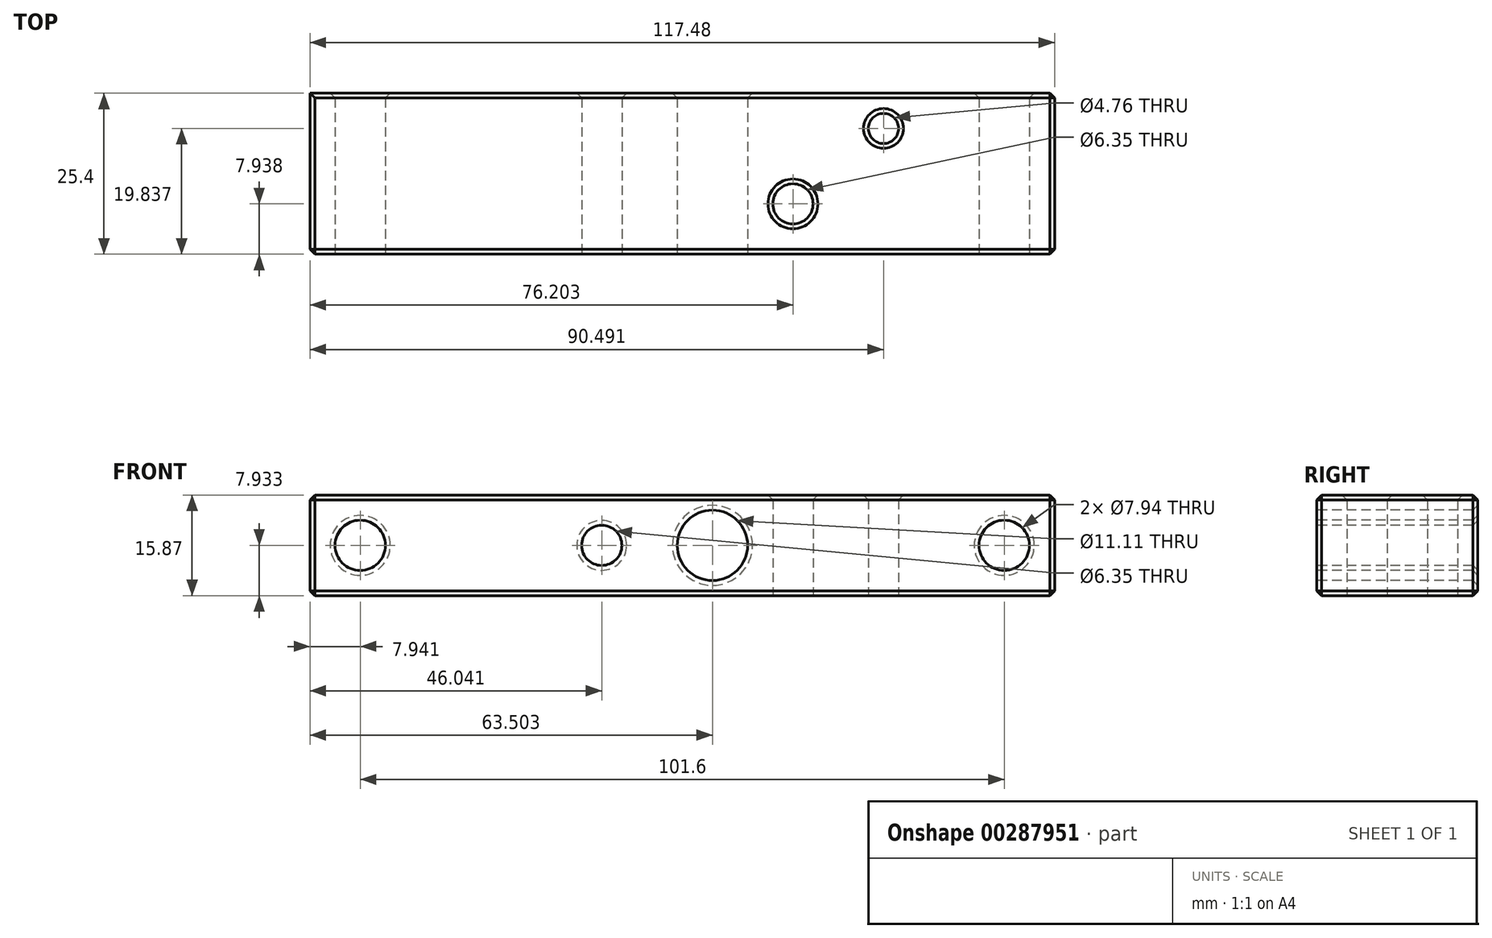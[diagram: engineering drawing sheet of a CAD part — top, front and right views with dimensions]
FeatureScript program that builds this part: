
annotation { "Feature Type Name" : "Feature", "Feature Type Description" : "" }
export const myFeature = defineFeature(function(context is Context, id is Id, definition is map)
    precondition{}
    {
        {
            var Q0;
            Q0=qCreatedBy(makeId("Front.planeOp"),FACE);
            var sketch = newSketch(context, id + "F0", { "sketchPlane" : qUnion([Q0])});
            skLineSegment(sketch, "E0.bottom", {"start": v(-99.14, 37.25) * mm, "end": v(18.34, 37.25) * mm});
            skLineSegment(sketch, "E0.top", {"start": v(-99.14, 21.38) * mm, "end": v(18.34, 21.38) * mm});
            skLineSegment(sketch, "E0.left", {"start": v(-99.14, 37.25) * mm, "end": v(-99.14, 21.38) * mm});
            skLineSegment(sketch, "E0.right", {"start": v(18.34, 37.25) * mm, "end": v(18.34, 21.38) * mm});
            skSolve(sketch);
        }
        {
            var Q0;
            Q0=makeQuery(id+"F0.imprint","IMPRINT",FACE,{"disambiguationData":[TD([[makeQuery(id+"F0.imprint","IMPRINT",EDGE,{"derivedFrom":sQuery(id+"F0.wireOp",EDGE,"E0.bottom")}),-1.0]])]});
            extrude(context, id + "F1", {"entities" : qUnion([Q0]), "depth" : 25.4 * mm, "offsetDistance" : 25.4 * mm});
        }
        {
            var Q0;
            Q0=makeQuery(id+"F1.opExtrude","CAP_FACE",FACE,{"disambiguationData":[OSD([sQuery(id+"F0.wireOp",EDGE,"E0.bottom"),sQuery(id+"F0.wireOp",EDGE,"E0.top"),sQuery(id+"F0.wireOp",EDGE,"E0.left"),sQuery(id+"F0.wireOp",EDGE,"E0.right")])],"isStart":false});
            var sketch = newSketch(context, id + "F2", { "sketchPlane" : qUnion([Q0])});
            skLineSegment(sketch, "E1", {"start": v(-120.74, 29.31) * mm, "end": v(39.47, 29.31) * mm, "construction": true});
            skCircle(sketch, "E2", {"center": v(-91.2, 29.31) * mm, "radius": 3.97 * mm});
            skCircle(sketch, "E3", {"center": v(-53.1, 29.31) * mm, "radius": 3.18 * mm});
            skCircle(sketch, "E4", {"center": v(-35.64, 29.31) * mm, "radius": 5.56 * mm});
            skCircle(sketch, "E5", {"center": v(10.4, 29.31) * mm, "radius": 3.97 * mm});
            skSolve(sketch);
        }
        {
            var Q0;
            Q0=makeQuery(id+"F2.imprint","IMPRINT",FACE,{"disambiguationData":[TD([[makeQuery(id+"F2.imprint","IMPRINT",EDGE,{"derivedFrom":sQuery(id+"F2.wireOp",EDGE,"E2")}),1.0]])]});
            var Q1;
            Q1=makeQuery(id+"F2.imprint","IMPRINT",FACE,{"disambiguationData":[TD([[makeQuery(id+"F2.imprint","IMPRINT",EDGE,{"derivedFrom":sQuery(id+"F2.wireOp",EDGE,"E3")}),1.0]])]});
            var Q2;
            Q2=makeQuery(id+"F2.imprint","IMPRINT",FACE,{"disambiguationData":[TD([[makeQuery(id+"F2.imprint","IMPRINT",EDGE,{"derivedFrom":sQuery(id+"F2.wireOp",EDGE,"E4")}),1.0]])]});
            var Q3;
            Q3=makeQuery(id+"F2.imprint","IMPRINT",FACE,{"disambiguationData":[TD([[makeQuery(id+"F2.imprint","IMPRINT",EDGE,{"derivedFrom":sQuery(id+"F2.wireOp",EDGE,"E5")}),1.0]])]});
            extrude(context, id + "F3", {"entities" : qUnion([Q0, Q1, Q2, Q3]), "operationType" : NewBodyOperationType.REMOVE, "oppositeDirection" : true, "depth" : 127 * mm, "offsetDistance" : 25.4 * mm});
        }
        {
            var Q0;
            Q0=makeQuery(id+"F1.opExtrude","SWEPT_FACE",FACE,{"disambiguationData":[OSD([sQuery(id+"F0.wireOp",EDGE,"E0.top")])]});
            var sketch = newSketch(context, id + "F4", { "sketchPlane" : qUnion([Q0])});
            skCircle(sketch, "E6", {"center": v(-22.94, 17.46) * mm, "radius": 3.18 * mm});
            skCircle(sketch, "E7", {"center": v(-8.65, 5.56) * mm, "radius": 2.38 * mm});
            skSolve(sketch);
        }
        {
            var Q0;
            Q0=makeQuery(id+"F4.imprint","IMPRINT",FACE,{"disambiguationData":[TD([[makeQuery(id+"F4.imprint","IMPRINT",EDGE,{"derivedFrom":sQuery(id+"F4.wireOp",EDGE,"E6")}),1.0]])]});
            var Q1;
            Q1=makeQuery(id+"F4.imprint","IMPRINT",FACE,{"disambiguationData":[TD([[makeQuery(id+"F4.imprint","IMPRINT",EDGE,{"derivedFrom":sQuery(id+"F4.wireOp",EDGE,"E7")}),1.0]])]});
            extrude(context, id + "F5", {"entities" : qUnion([Q0, Q1]), "operationType" : NewBodyOperationType.REMOVE, "oppositeDirection" : true, "depth" : 25.4 * mm, "offsetDistance" : 25.4 * mm});
        }
        {
            var Q0;
            Q0=makeQuery(id+"F1.opExtrude","CAP_EDGE",EDGE,{"disambiguationData":[OSD([sQuery(id+"F0.wireOp",EDGE,"E0.top")])],"isStart":false});
            var Q1;
            Q1=makeQuery(id+"F1.opExtrude","CAP_EDGE",EDGE,{"disambiguationData":[OSD([sQuery(id+"F0.wireOp",EDGE,"E0.bottom")])],"isStart":false});
            var Q2;
            Q2=makeQuery(id+"F1.opExtrude","CAP_EDGE",EDGE,{"disambiguationData":[OSD([sQuery(id+"F0.wireOp",EDGE,"E0.right")])],"isStart":false});
            var Q3;
            Q3=makeQuery(id+"F3.boolean.opBoolean","COPY",EDGE,{"derivedFrom":makeQuery(id+"F3.opExtrude","CAP_EDGE",EDGE,{"disambiguationData":[OSD([sQuery(id+"F2.wireOp",EDGE,"E5")])],"isStart":true})});
            var Q4;
            Q4=makeQuery(id+"F3.boolean.opBoolean","COPY",EDGE,{"derivedFrom":makeQuery(id+"F3.opExtrude","CAP_EDGE",EDGE,{"disambiguationData":[OSD([sQuery(id+"F2.wireOp",EDGE,"E4")])],"isStart":true})});
            var Q5;
            Q5=makeQuery(id+"F3.boolean.opBoolean","COPY",EDGE,{"derivedFrom":makeQuery(id+"F3.opExtrude","CAP_EDGE",EDGE,{"disambiguationData":[OSD([sQuery(id+"F2.wireOp",EDGE,"E3")])],"isStart":true})});
            var Q6;
            Q6=makeQuery(id+"F1.opExtrude","CAP_EDGE",EDGE,{"disambiguationData":[OSD([sQuery(id+"F0.wireOp",EDGE,"E0.left")])],"isStart":false});
            var Q7;
            Q7=makeQuery(id+"F3.boolean.opBoolean","COPY",EDGE,{"derivedFrom":makeQuery(id+"F3.opExtrude","CAP_EDGE",EDGE,{"disambiguationData":[OSD([sQuery(id+"F2.wireOp",EDGE,"E2")])],"isStart":true})});
            var Q8;
            Q8=makeQuery(id+"F1.opExtrude","SWEPT_EDGE",EDGE,{"disambiguationData":[OSD([sQuery(id+"F0.wireOp",EDGE,"E0.top"),sQuery(id+"F0.wireOp",EDGE,"E0.left")])]});
            var Q9;
            Q9=makeQuery(id+"F1.opExtrude","CAP_EDGE",EDGE,{"disambiguationData":[OSD([sQuery(id+"F0.wireOp",EDGE,"E0.top")])],"isStart":true});
            var Q10;
            Q10=makeQuery(id+"F5.boolean.opBoolean","COPY",EDGE,{"derivedFrom":makeQuery(id+"F5.opExtrude","CAP_EDGE",EDGE,{"disambiguationData":[OSD([sQuery(id+"F4.wireOp",EDGE,"E6")])],"isStart":true})});
            var Q11;
            Q11=makeQuery(id+"F5.boolean.opBoolean","COPY",EDGE,{"derivedFrom":makeQuery(id+"F5.opExtrude","CAP_EDGE",EDGE,{"disambiguationData":[OSD([sQuery(id+"F4.wireOp",EDGE,"E7")])],"isStart":true})});
            var Q12;
            Q12=makeQuery(id+"F1.opExtrude","SWEPT_EDGE",EDGE,{"disambiguationData":[OSD([sQuery(id+"F0.wireOp",EDGE,"E0.top"),sQuery(id+"F0.wireOp",EDGE,"E0.right")])]});
            var Q13;
            Q13=makeQuery(id+"F1.opExtrude","SWEPT_EDGE",EDGE,{"disambiguationData":[OSD([sQuery(id+"F0.wireOp",EDGE,"E0.bottom"),sQuery(id+"F0.wireOp",EDGE,"E0.right")])]});
            var Q14;
            Q14=makeQuery(id+"F1.opExtrude","CAP_EDGE",EDGE,{"disambiguationData":[OSD([sQuery(id+"F0.wireOp",EDGE,"E0.right")])],"isStart":true});
            var Q15;
            Q15=makeQuery(id+"F5.boolean.opBoolean","INTERSECT",EDGE,{"derivedFrom":[makeQuery(id+"F1.opExtrude","SWEPT_FACE",FACE,{"disambiguationData":[OSD([sQuery(id+"F0.wireOp",EDGE,"E0.bottom")])]}),makeQuery(id+"F5.opExtrude","SWEPT_FACE",FACE,{"disambiguationData":[OSD([sQuery(id+"F4.wireOp",EDGE,"E6")])]})]});
            var Q16;
            Q16=makeQuery(id+"F5.boolean.opBoolean","INTERSECT",EDGE,{"derivedFrom":[makeQuery(id+"F1.opExtrude","SWEPT_FACE",FACE,{"disambiguationData":[OSD([sQuery(id+"F0.wireOp",EDGE,"E0.bottom")])]}),makeQuery(id+"F5.opExtrude","SWEPT_FACE",FACE,{"disambiguationData":[OSD([sQuery(id+"F4.wireOp",EDGE,"E7")])]})]});
            var Q17;
            Q17=makeQuery(id+"F1.opExtrude","CAP_EDGE",EDGE,{"disambiguationData":[OSD([sQuery(id+"F0.wireOp",EDGE,"E0.bottom")])],"isStart":true});
            var Q18;
            Q18=makeQuery(id+"F1.opExtrude","SWEPT_EDGE",EDGE,{"disambiguationData":[OSD([sQuery(id+"F0.wireOp",EDGE,"E0.bottom"),sQuery(id+"F0.wireOp",EDGE,"E0.left")])]});
            var Q19;
            Q19=makeQuery(id+"F3.boolean.opBoolean","INTERSECT",EDGE,{"derivedFrom":[makeQuery(id+"F1.opExtrude","CAP_FACE",FACE,{"disambiguationData":[OSD([sQuery(id+"F0.wireOp",EDGE,"E0.bottom"),sQuery(id+"F0.wireOp",EDGE,"E0.top"),sQuery(id+"F0.wireOp",EDGE,"E0.left"),sQuery(id+"F0.wireOp",EDGE,"E0.right")])],"isStart":true}),makeQuery(id+"F3.opExtrude","SWEPT_FACE",FACE,{"disambiguationData":[OSD([sQuery(id+"F2.wireOp",EDGE,"E4")])]})]});
            var Q20;
            Q20=makeQuery(id+"F3.boolean.opBoolean","INTERSECT",EDGE,{"derivedFrom":[makeQuery(id+"F1.opExtrude","CAP_FACE",FACE,{"disambiguationData":[OSD([sQuery(id+"F0.wireOp",EDGE,"E0.bottom"),sQuery(id+"F0.wireOp",EDGE,"E0.top"),sQuery(id+"F0.wireOp",EDGE,"E0.left"),sQuery(id+"F0.wireOp",EDGE,"E0.right")])],"isStart":true}),makeQuery(id+"F3.opExtrude","SWEPT_FACE",FACE,{"disambiguationData":[OSD([sQuery(id+"F2.wireOp",EDGE,"E3")])]})]});
            var Q21;
            Q21=makeQuery(id+"F3.boolean.opBoolean","INTERSECT",EDGE,{"derivedFrom":[makeQuery(id+"F1.opExtrude","CAP_FACE",FACE,{"disambiguationData":[OSD([sQuery(id+"F0.wireOp",EDGE,"E0.bottom"),sQuery(id+"F0.wireOp",EDGE,"E0.top"),sQuery(id+"F0.wireOp",EDGE,"E0.left"),sQuery(id+"F0.wireOp",EDGE,"E0.right")])],"isStart":true}),makeQuery(id+"F3.opExtrude","SWEPT_FACE",FACE,{"disambiguationData":[OSD([sQuery(id+"F2.wireOp",EDGE,"E5")])]})]});
            var Q22;
            Q22=makeQuery(id+"F3.boolean.opBoolean","INTERSECT",EDGE,{"derivedFrom":[makeQuery(id+"F1.opExtrude","CAP_FACE",FACE,{"disambiguationData":[OSD([sQuery(id+"F0.wireOp",EDGE,"E0.bottom"),sQuery(id+"F0.wireOp",EDGE,"E0.top"),sQuery(id+"F0.wireOp",EDGE,"E0.left"),sQuery(id+"F0.wireOp",EDGE,"E0.right")])],"isStart":true}),makeQuery(id+"F3.opExtrude","SWEPT_FACE",FACE,{"disambiguationData":[OSD([sQuery(id+"F2.wireOp",EDGE,"E2")])]})]});
            chamfer(context, id + "F6", {"entities" : qUnion([Q0, Q1, Q2, Q3, Q4, Q5, Q6, Q7, Q8, Q9, Q10, Q11, Q12, Q13, Q14, Q15, Q16, Q17, Q18, Q19, Q20, Q21, Q22]), "chamferType" : ChamferType.OFFSET_ANGLE, "width" : 0.76 * mm, "oppositeDirection" : false, "angle" : 45 * degree, "tangentPropagation" : true});
        }
    });
